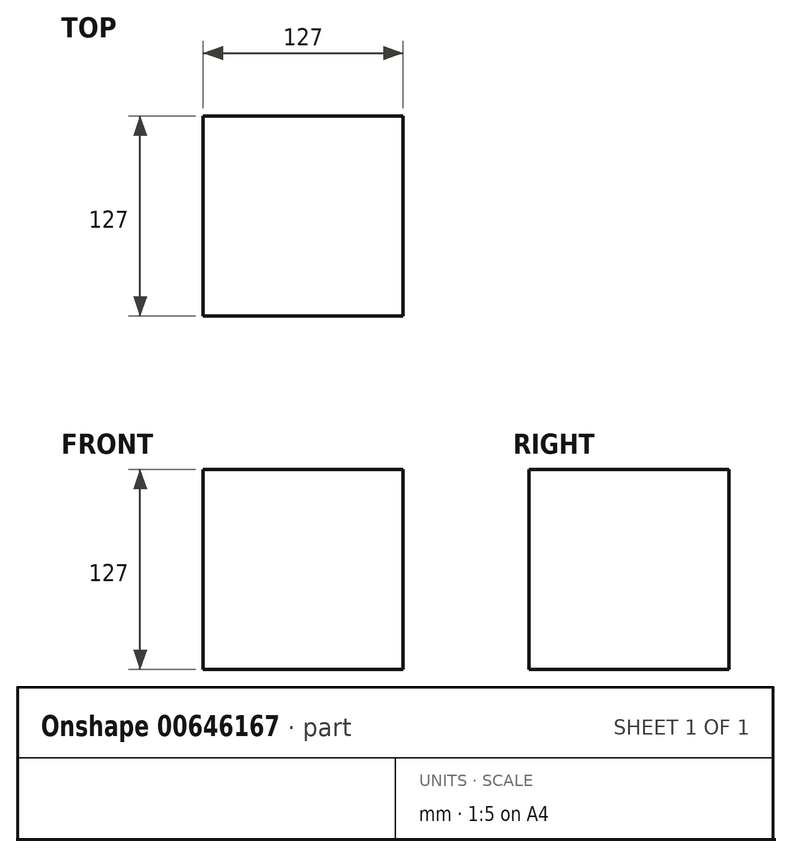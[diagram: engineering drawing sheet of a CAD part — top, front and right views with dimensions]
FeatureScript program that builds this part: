
annotation { "Feature Type Name" : "Feature", "Feature Type Description" : "" }
export const myFeature = defineFeature(function(context is Context, id is Id, definition is map)
    precondition{}
    {
        {
            var Q0;
            Q0=qCreatedBy(makeId("Right.planeOp"),FACE);
            var sketch = newSketch(context, id + "F0", { "sketchPlane" : qUnion([Q0])});
            skLineSegment(sketch, "E0.bottom", {"start": v(61.2, 59.36) * mm, "end": v(-65.8, 59.36) * mm});
            skLineSegment(sketch, "E0.top", {"start": v(61.2, -67.64) * mm, "end": v(-65.8, -67.64) * mm});
            skLineSegment(sketch, "E0.left", {"start": v(61.2, 59.36) * mm, "end": v(61.2, -67.64) * mm});
            skLineSegment(sketch, "E0.right", {"start": v(-65.8, 59.36) * mm, "end": v(-65.8, -67.64) * mm});
            skSolve(sketch);
        }
        {
            var Q0;
            Q0 = qSketchRegion(id + "F0", true);
            extrude(context, id + "F1", {"entities" : qUnion([Q0]), "depth" : 63.5 * mm, "offsetDistance" : 25.4 * mm});
        }
        {
            var Q0;
            Q0=makeQuery(id+"F1.opExtrude","CAP_FACE",FACE,{"disambiguationData":[OSD([sQuery(id+"F0.wireOp",EDGE,"E0.bottom"),sQuery(id+"F0.wireOp",EDGE,"E0.top"),sQuery(id+"F0.wireOp",EDGE,"E0.left"),sQuery(id+"F0.wireOp",EDGE,"E0.right")])],"isStart":true});
            extrude(context, id + "F2", {"entities" : qUnion([Q0]), "operationType" : NewBodyOperationType.ADD, "depth" : 63.5 * mm, "offsetDistance" : 25.4 * mm});
        }
    });
